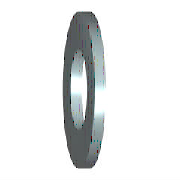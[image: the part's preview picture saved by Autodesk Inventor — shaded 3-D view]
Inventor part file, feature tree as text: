
AUTODESK INVENTOR PART (.ipt)
format: ipt  version: 2020 (Build 240168000, 168)  size: 105,472 bytes
history: native  units: mm (DEFAULTED — no unit token found)
features: extrude x1, other x1, plane x1, sketch x1
ambient origin geometry x7: Origin, YZ Plane, XY Plane, X Axis, Y Axis, Z Axis, Center Point
bodies: Solid1 (feature_tree)
feature tree (4):
  extrude  "Körper"  Depth=1.6mm
  other  "Work Axis1"
  plane  "Work Plane1"
  sketch  "Skizze"  dims[d0=6.4mm d1=18.0mm d2=1.6mm d3=0.0mm d4=0.0mm d5=0.0mm d6=0.0mm d7=0.0mm]
